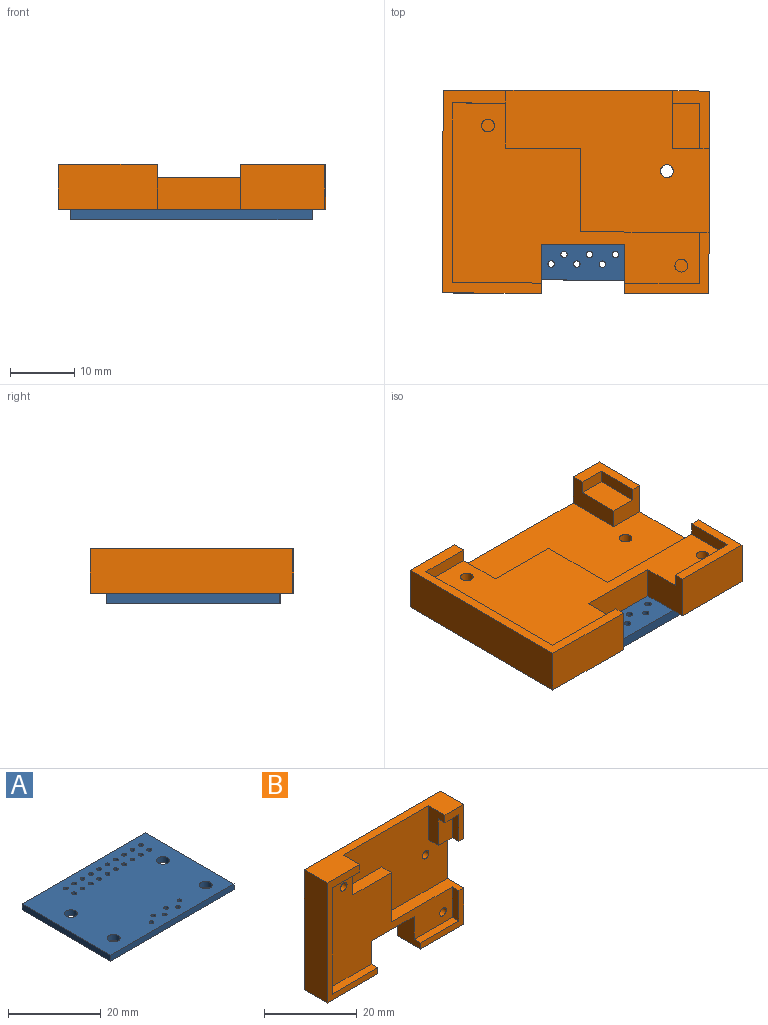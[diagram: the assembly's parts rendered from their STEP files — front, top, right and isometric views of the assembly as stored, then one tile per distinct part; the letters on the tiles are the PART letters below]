
ASSEMBLY  parts=2 mates=1
PART A: 36 faces, bbox 37.6x27x1.6 mm
  f0: cylinder r=0.51mm len=1.57mm, axis (0,0,1), area 5mm2, adj f34,f35
  f1: cylinder r=0.51mm len=1.57mm, axis (0,0,1), area 5mm2, adj f34,f35
  f2: cylinder r=0.51mm len=1.57mm, axis (0,0,1), area 5mm2, adj f34,f35
  f3: cylinder r=0.51mm len=1.57mm, axis (0,0,1), area 5mm2, adj f34,f35
  f4: cylinder r=0.51mm len=1.57mm, axis (0,0,1), area 5mm2, adj f34,f35
  f5: cylinder r=0.51mm len=1.57mm, axis (0,0,1), area 5mm2, adj f34,f35
  f6: cylinder r=0.5mm len=1.57mm, axis (0,0,1), area 4.9mm2, adj f34,f35
  f7: cylinder r=0.51mm len=1.57mm, axis (0,0,1), area 5mm2, adj f34,f35
  f8: cylinder r=0.51mm len=1.57mm, axis (0,0,1), area 5mm2, adj f34,f35
  f9: cylinder r=0.51mm len=1.57mm, axis (0,0,1), area 5mm2, adj f34,f35
  f10: cylinder r=0.5mm len=1.57mm, axis (0,0,1), area 4.9mm2, adj f34,f35
  f11: cylinder r=0.5mm len=1.57mm, axis (0,0,1), area 4.9mm2, adj f34,f35
  f12: cylinder r=0.5mm len=1.57mm, axis (0,0,1), area 4.9mm2, adj f34,f35
  f13: cylinder r=0.5mm len=1.57mm, axis (0,0,1), area 4.9mm2, adj f34,f35
  f14: cylinder r=0.5mm len=1.57mm, axis (0,0,1), area 4.9mm2, adj f34,f35
  f15: cylinder r=0.51mm len=1.57mm, axis (0,0,1), area 5mm2, adj f34,f35
  f16: cylinder r=0.51mm len=1.57mm, axis (0,0,1), area 5mm2, adj f34,f35
  f17: cylinder r=0.51mm len=1.57mm, axis (0,0,1), area 5mm2, adj f34,f35
  f18: cylinder r=0.51mm len=1.57mm, axis (0,0,1), area 5mm2, adj f34,f35
  f19: cylinder r=0.51mm len=1.57mm, axis (0,0,1), area 5mm2, adj f34,f35
  f20: cylinder r=0.51mm len=1.57mm, axis (0,0,1), area 5mm2, adj f34,f35
  f21: cylinder r=0.51mm len=1.57mm, axis (0,0,1), area 5mm2, adj f34,f35
  f22: cylinder r=0.51mm len=1.57mm, axis (0,0,1), area 5mm2, adj f34,f35
  f23: cylinder r=0.51mm len=1.57mm, axis (0,0,1), area 5mm2, adj f34,f35
  f24: cylinder r=0.51mm len=1.57mm, axis (0,0,1), area 5mm2, adj f34,f35
  f25: cylinder r=0.51mm len=1.57mm, axis (0,0,1), area 5mm2, adj f34,f35
  f26: cylinder r=1.4mm len=2.8mm, axis (0,0,1), area 13.8mm2, adj f34,f35
  f27: cylinder r=1.4mm len=2.8mm, axis (0,0,1), area 13.8mm2, adj f34,f35
  f28: cylinder r=1.4mm len=2.8mm, axis (0,0,1), area 13.8mm2, adj f34,f35
  f29: cylinder r=1.4mm len=2.8mm, axis (0,0,1), area 13.8mm2, adj f34,f35
  f30: plane 37.5x1.57mm, normal (0,1,0), area 58.9mm2, adj f31,f33,f34,f35
  f31: plane 27x1.57mm, normal (1,0,0), area 42.4mm2, adj f30,f32,f34,f35
  f32: plane 37.6x1.57mm, normal (0,-1,0), area 59mm2, adj f31,f33,f34,f35
  f33: plane 27x1.57mm, normal (-1,0,0), area 42.4mm2, adj f30,f32,f34,f35
  f34: plane 37.6x27mm, normal (0,0,1), area 968.3mm2, adj f0,f1,f2,f3,f4,f5,f6,f7
  f35: plane 37.6x27mm, normal (0,0,-1), area 968.3mm2, adj f0,f1,f2,f3,f4,f5,f6,f7
PART B: 39 faces, bbox 41.5x7x31.6 mm
  f0: plane 15.41x7mm, normal (0,0,-1), area 107.9mm2, adj f1,f11,f23,f25
  f1: plane 31.59x15.41mm, normal (0,-1,0), area 86.1mm2, adj f0,f18,f20,f21,f22,f23,f25,f33
  f2: plane 11.6x2mm, normal (0,0,1), area 23.2mm2, adj f3,f5,f8,f27
  f3: plane 38.5x28mm, normal (0,-1,0), area 541.7mm2, adj f2,f8,f18,f20,f22,f25,f26,f27
  f4: cylinder r=1mm len=2mm, axis (0,1,0), area 12.6mm2, adj f11,f32
  f5: plane 13.1x9.59mm, normal (0,-1,0), area 32.8mm2, adj f2,f8,f9,f19,f27,f36
  f6: plane 9x5.72mm, normal (0,-1,0), area 21.9mm2, adj f7,f9,f21,f24,f37,f38
  f7: plane 4.22x2mm, normal (0,0,-1), area 8.4mm2, adj f6,f10,f24,f38
  f8: plane 8x2mm, normal (-1,0,0), area 16mm2, adj f2,f3,f5,f36
  f9: plane 31.59x7mm, normal (1,0,0), area 156.1mm2, adj f5,f6,f11,f19,f21,f32,f36,f37
  f10: plane 7x4.22mm, normal (0,-1,0), area 29.5mm2, adj f7,f24,f37,f38
  f11: plane 41.5x31.59mm, normal (0,1,0), area 1199.8mm2, adj f0,f4,f9,f12,f14,f16,f19,f21
  f12: cylinder r=1mm len=3mm, axis (0,1,0), area 18.8mm2, adj f11,f13
  f13: plane 2x2mm, normal (0,1,0), area 3.1mm2, adj f12
  f14: cylinder r=1mm len=3mm, axis (0,1,0), area 18.8mm2, adj f11,f15
  f15: plane 2x2mm, normal (0,1,0), area 3.1mm2, adj f14
  f16: cylinder r=1mm len=3mm, axis (0,1,0), area 18.8mm2, adj f11,f17
  f17: plane 2x2mm, normal (0,1,0), area 3.1mm2, adj f16
  f18: plane 13.91x2mm, normal (0,0,1), area 27.8mm2, adj f1,f3,f22,f25
  f19: plane 13.1x7mm, normal (0,0,-1), area 91.7mm2, adj f5,f9,f11,f27
  f20: plane 8.28x2mm, normal (0,0,-1), area 16.6mm2, adj f1,f3,f22,f33
  f21: plane 41.5x7mm, normal (0,0,1), area 160.5mm2, adj f1,f6,f9,f11,f23,f32,f33,f38
  f22: plane 28x2mm, normal (1,0,0), area 56mm2, adj f1,f3,f18,f20
  f23: plane 31.59x7mm, normal (-1,0,0), area 221.1mm2, adj f0,f1,f11,f21
  f24: plane 7x2mm, normal (-1,0,0), area 14mm2, adj f6,f7,f10,f37
  f25: plane 7.6x7mm, normal (1,0,0), area 41.2mm2, adj f0,f1,f3,f11,f18,f26
  f26: plane 12.99x5mm, normal (0,0,-1), area 64.9mm2, adj f3,f11,f25,f27
  f27: plane 7.6x7mm, normal (-1,0,0), area 41.2mm2, adj f2,f3,f5,f11,f19,f26
  f28: cylinder r=1mm len=3mm, axis (0,-1,0), area 18.8mm2, adj f3,f29
  f29: plane 2x2mm, normal (0,-1,0), area 3.1mm2, adj f28
  f30: cylinder r=1mm len=3mm, axis (0,-1,0), area 18.8mm2, adj f3,f31
  f31: plane 2x2mm, normal (0,-1,0), area 3.1mm2, adj f30
  f32: plane 31.72x22mm, normal (0,-1,0), area 490.9mm2, adj f4,f9,f21,f33,f34,f35,f36,f37
  f33: plane 9x5mm, normal (1,0,0), area 31mm2, adj f1,f3,f20,f21,f32,f34
  f34: plane 11.72x3mm, normal (0,0,1), area 35.2mm2, adj f3,f32,f33,f35
  f35: plane 13x3mm, normal (1,0,0), area 39mm2, adj f3,f32,f34,f36
  f36: plane 20x5mm, normal (0,0,1), area 63mm2, adj f3,f5,f8,f9,f32,f35
  f37: plane 5.72x5mm, normal (0,0,-1), area 20.2mm2, adj f6,f9,f10,f24,f32,f38
  f38: plane 9x5mm, normal (-1,0,0), area 31mm2, adj f6,f7,f10,f21,f32,f37
PLACE A rot(axis=(0,0,-1),0.2deg) t=(-0.05,0,0)mm
PLACE B rot(axis=(-1,0,0),90deg) t=(18.85,13.43,1.57)mm fixed
MATE planar A.f34 <-> B.f11  axis (0,0,1) through (18.76,13.39,1.57)mm
